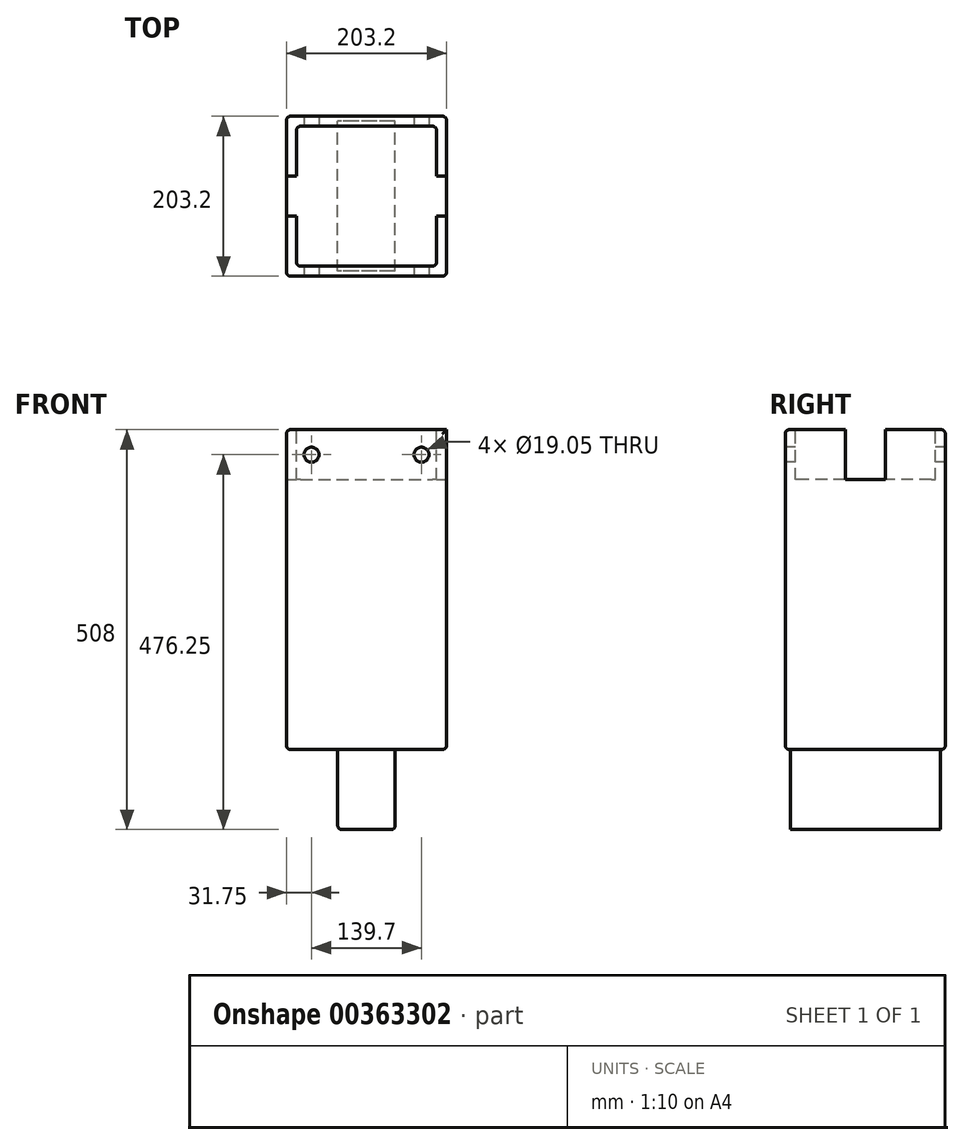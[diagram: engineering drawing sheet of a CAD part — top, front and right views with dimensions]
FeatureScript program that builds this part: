
annotation { "Feature Type Name" : "Feature", "Feature Type Description" : "" }
export const myFeature = defineFeature(function(context is Context, id is Id, definition is map)
    precondition{}
    {
        {
            var Q0;
            Q0=qCreatedBy(makeId("Top.planeOp"),FACE);
            var sketch = newSketch(context, id + "F0", { "sketchPlane" : qUnion([Q0])});
            skLineSegment(sketch, "E0.bottom", {"start": v(101.6, -101.6) * mm, "end": v(-101.6, -101.6) * mm});
            skLineSegment(sketch, "E0.top", {"start": v(101.6, 101.6) * mm, "end": v(-101.6, 101.6) * mm});
            skLineSegment(sketch, "E0.left", {"start": v(101.6, -101.6) * mm, "end": v(101.6, 101.6) * mm});
            skLineSegment(sketch, "E0.right", {"start": v(-101.6, -101.6) * mm, "end": v(-101.6, 101.6) * mm});
            skPoint(sketch, "E0.middle", {"position": v(0, 0) * mm});
            skSolve(sketch);
        }
        {
            var Q0;
            Q0=makeQuery(id+"F0.imprint","IMPRINT",FACE,{"disambiguationData":[TD([[makeQuery(id+"F0.imprint","IMPRINT",EDGE,{"derivedFrom":sQuery(id+"F0.wireOp",EDGE,"E0.bottom")}),-1.0]])]});
            extrude(context, id + "F1", {"entities" : qUnion([Q0]), "depth" : 406.4 * mm});
        }
        {
            var Q0;
            Q0=makeQuery(id+"F1.opExtrude","CAP_FACE",FACE,{"disambiguationData":[OSD([sQuery(id+"F0.wireOp",EDGE,"E0.bottom"),sQuery(id+"F0.wireOp",EDGE,"E0.top"),sQuery(id+"F0.wireOp",EDGE,"E0.left"),sQuery(id+"F0.wireOp",EDGE,"E0.right")])],"isStart":false});
            var sketch = newSketch(context, id + "F2", { "sketchPlane" : qUnion([Q0])});
            skLineSegment(sketch, "E1.0", {"start": v(101.6, -101.6) * mm, "end": v(101.6, 101.6) * mm});
            skLineSegment(sketch, "E1.2", {"start": v(101.6, 101.6) * mm, "end": v(-101.6, 101.6) * mm});
            skLineSegment(sketch, "E2.bottom", {"start": v(-88.9, 88.9) * mm, "end": v(88.9, 88.9) * mm});
            skLineSegment(sketch, "E2.top", {"start": v(-88.9, -88.9) * mm, "end": v(88.9, -88.9) * mm});
            skLineSegment(sketch, "E2.left", {"start": v(-88.9, 88.9) * mm, "end": v(-88.9, -88.9) * mm});
            skLineSegment(sketch, "E2.right", {"start": v(88.9, 88.9) * mm, "end": v(88.9, -88.9) * mm});
            skSolve(sketch);
        }
        {
            var Q0;
            Q0=makeQuery(id+"F2.imprint","IMPRINT",FACE,{"disambiguationData":[TD([[makeQuery(id+"F2.imprint","IMPRINT",EDGE,{"derivedFrom":sQuery(id+"F2.wireOp",EDGE,"E2.bottom")}),-1.0]])]});
            extrude(context, id + "F3", {"entities" : qUnion([Q0]), "operationType" : NewBodyOperationType.REMOVE, "oppositeDirection" : true, "depth" : 63.5 * mm});
        }
        {
            var Q0;
            Q0=makeQuery(id+"F1.opExtrude","SWEPT_FACE",FACE,{"disambiguationData":[OSD([sQuery(id+"F0.wireOp",EDGE,"E0.bottom")])]});
            var sketch = newSketch(context, id + "F4", { "sketchPlane" : qUnion([Q0])});
            skCircle(sketch, "E3", {"center": v(-69.85, 374.65) * mm, "radius": 9.53 * mm});
            skCircle(sketch, "E4", {"center": v(69.85, 374.65) * mm, "radius": 9.53 * mm});
            skSolve(sketch);
        }
        {
            var Q0;
            Q0=makeQuery(id+"F4.imprint","IMPRINT",FACE,{"disambiguationData":[TD([[makeQuery(id+"F4.imprint","IMPRINT",EDGE,{"derivedFrom":sQuery(id+"F4.wireOp",EDGE,"E3")}),1.0]])]});
            var Q1;
            Q1=makeQuery(id+"F4.imprint","IMPRINT",FACE,{"disambiguationData":[TD([[makeQuery(id+"F4.imprint","IMPRINT",EDGE,{"derivedFrom":sQuery(id+"F4.wireOp",EDGE,"E4")}),1.0]])]});
            extrude(context, id + "F5", {"entities" : qUnion([Q0, Q1]), "operationType" : NewBodyOperationType.REMOVE, "oppositeDirection" : true, "depth" : 205.74 * mm});
        }
        {
            var Q0;
            Q0=makeQuery(id+"F1.opExtrude","SWEPT_FACE",FACE,{"disambiguationData":[OSD([sQuery(id+"F0.wireOp",EDGE,"E0.left")])]});
            var sketch = newSketch(context, id + "F6", { "sketchPlane" : qUnion([Q0])});
            skLineSegment(sketch, "E5.bottom", {"start": v(-25.4, 406.4) * mm, "end": v(25.4, 406.4) * mm});
            skLineSegment(sketch, "E5.top", {"start": v(-25.4, 342.9) * mm, "end": v(25.4, 342.9) * mm});
            skLineSegment(sketch, "E5.left", {"start": v(-25.4, 406.4) * mm, "end": v(-25.4, 342.9) * mm});
            skLineSegment(sketch, "E5.right", {"start": v(25.4, 406.4) * mm, "end": v(25.4, 342.9) * mm});
            skPoint(sketch, "E5.middle", {"position": v(0, 374.65) * mm});
            skPoint(sketch, "E5.middle.positionSnap0", {"position": v(0, 406.4) * mm});
            skPoint(sketch, "E5.centerSnap0", {"position": v(0, 406.4) * mm});
            skSolve(sketch);
        }
        {
            var Q0;
            Q0 = qSketchRegion(id + "F6", true);
            extrude(context, id + "F7", {"entities" : qUnion([Q0]), "operationType" : NewBodyOperationType.REMOVE, "oppositeDirection" : true, "depth" : 228.6 * mm});
        }
        {
            var Q0;
            Q0=makeQuery(id+"F0.imprint","IMPRINT",FACE,{"disambiguationData":[TD([[makeQuery(id+"F0.imprint","IMPRINT",EDGE,{"derivedFrom":sQuery(id+"F0.wireOp",EDGE,"E0.bottom")}),-1.0]])]});
            var sketch = newSketch(context, id + "F8", { "sketchPlane" : qUnion([Q0])});
            skLineSegment(sketch, "E6.bottom", {"start": v(36.52, -95.25) * mm, "end": v(-36.52, -95.25) * mm});
            skLineSegment(sketch, "E6.top", {"start": v(36.52, 95.25) * mm, "end": v(-36.52, 95.25) * mm});
            skLineSegment(sketch, "E6.left", {"start": v(36.52, -95.25) * mm, "end": v(36.52, 95.25) * mm});
            skLineSegment(sketch, "E6.right", {"start": v(-36.52, -95.25) * mm, "end": v(-36.52, 95.25) * mm});
            skPoint(sketch, "E6.middle", {"position": v(0, 0) * mm});
            skSolve(sketch);
        }
        {
            var Q0;
            Q0=makeQuery(id+"F8.imprint","IMPRINT",FACE,{"disambiguationData":[TD([[makeQuery(id+"F8.imprint","IMPRINT",EDGE,{"derivedFrom":sQuery(id+"F8.wireOp",EDGE,"E6.bottom")}),-1.0]])]});
            extrude(context, id + "F9", {"entities" : qUnion([Q0]), "operationType" : NewBodyOperationType.ADD, "depth" : -101.6 * mm});
        }
        {
            var Q0;
            Q0=makeQuery(id+"F1.opExtrude","SWEPT_EDGE",EDGE,{"disambiguationData":[OSD([sQuery(id+"F0.wireOp",EDGE,"E0.top"),sQuery(id+"F0.wireOp",EDGE,"E0.right")])]});
            var Q1;
            Q1=makeQuery(id+"F1.opExtrude","SWEPT_EDGE",EDGE,{"disambiguationData":[OSD([sQuery(id+"F0.wireOp",EDGE,"E0.bottom"),sQuery(id+"F0.wireOp",EDGE,"E0.right")])]});
            var Q2;
            Q2=makeQuery(id+"F1.opExtrude","SWEPT_EDGE",EDGE,{"disambiguationData":[OSD([sQuery(id+"F0.wireOp",EDGE,"E0.top"),sQuery(id+"F0.wireOp",EDGE,"E0.left")])]});
            var Q3;
            {var subQ0=sQuery(id+"F0.wireOp",EDGE,"E0.left");var subQ1=sQuery(id+"F0.wireOp",EDGE,"E0.top");Q3=makeQuery(id+"F7.boolean.opBoolean","SPLIT",EDGE,{"disambiguationData":[TD([makeQuery(id+"F1.opExtrude","SWEPT_FACE",FACE,{"disambiguationData":[OSD([subQ1])]})])],"derivedFrom":makeQuery(id+"F1.opExtrude","CAP_EDGE",EDGE,{"disambiguationData":[OSD([subQ0])],"isStart":false})});}
            var Q4;
            Q4=makeQuery(id+"F1.opExtrude","CAP_EDGE",EDGE,{"disambiguationData":[OSD([sQuery(id+"F0.wireOp",EDGE,"E0.top")])],"isStart":false});
            var Q5;
            {var subQ0=sQuery(id+"F0.wireOp",EDGE,"E0.right");var subQ1=sQuery(id+"F0.wireOp",EDGE,"E0.top");Q5=makeQuery(id+"F7.boolean.opBoolean","SPLIT",EDGE,{"disambiguationData":[TD([makeQuery(id+"F1.opExtrude","SWEPT_FACE",FACE,{"disambiguationData":[OSD([subQ1])]})])],"derivedFrom":makeQuery(id+"F1.opExtrude","CAP_EDGE",EDGE,{"disambiguationData":[OSD([subQ0])],"isStart":false})});}
            var Q6;
            {var subQ0=sQuery(id+"F0.wireOp",EDGE,"E0.bottom");var subQ1=sQuery(id+"F0.wireOp",EDGE,"E0.right");Q6=makeQuery(id+"F7.boolean.opBoolean","SPLIT",EDGE,{"disambiguationData":[TD([makeQuery(id+"F1.opExtrude","SWEPT_FACE",FACE,{"disambiguationData":[OSD([subQ0])]})])],"derivedFrom":makeQuery(id+"F1.opExtrude","CAP_EDGE",EDGE,{"disambiguationData":[OSD([subQ1])],"isStart":false})});}
            var Q7;
            Q7=makeQuery(id+"F1.opExtrude","CAP_EDGE",EDGE,{"disambiguationData":[OSD([sQuery(id+"F0.wireOp",EDGE,"E0.bottom")])],"isStart":false});
            var Q8;
            Q8=makeQuery(id+"F1.opExtrude","SWEPT_EDGE",EDGE,{"disambiguationData":[OSD([sQuery(id+"F0.wireOp",EDGE,"E0.bottom"),sQuery(id+"F0.wireOp",EDGE,"E0.left")])]});
            var Q9;
            Q9=makeQuery(id+"F1.opExtrude","CAP_EDGE",EDGE,{"disambiguationData":[OSD([sQuery(id+"F0.wireOp",EDGE,"E0.left")])],"isStart":true});
            var Q10;
            Q10=makeQuery(id+"F1.opExtrude","CAP_EDGE",EDGE,{"disambiguationData":[OSD([sQuery(id+"F0.wireOp",EDGE,"E0.bottom")])],"isStart":true});
            var Q11;
            Q11=makeQuery(id+"F1.opExtrude","CAP_EDGE",EDGE,{"disambiguationData":[OSD([sQuery(id+"F0.wireOp",EDGE,"E0.top")])],"isStart":true});
            var Q12;
            Q12=makeQuery(id+"F1.opExtrude","CAP_EDGE",EDGE,{"disambiguationData":[OSD([sQuery(id+"F0.wireOp",EDGE,"E0.right")])],"isStart":true});
            var Q13;
            Q13=makeQuery(id+"F3.boolean.opBoolean","COPY",EDGE,{"derivedFrom":makeQuery(id+"F3.opExtrude","SWEPT_EDGE",EDGE,{"disambiguationData":[OSD([sQuery(id+"F2.wireOp",EDGE,"E2.top"),sQuery(id+"F2.wireOp",EDGE,"E2.left")])]})});
            var Q14;
            Q14=makeQuery(id+"F3.boolean.opBoolean","COPY",EDGE,{"derivedFrom":makeQuery(id+"F3.opExtrude","SWEPT_EDGE",EDGE,{"disambiguationData":[OSD([sQuery(id+"F2.wireOp",EDGE,"E2.bottom"),sQuery(id+"F2.wireOp",EDGE,"E2.left")])]})});
            var Q15;
            Q15=makeQuery(id+"F3.boolean.opBoolean","COPY",EDGE,{"derivedFrom":makeQuery(id+"F3.opExtrude","SWEPT_EDGE",EDGE,{"disambiguationData":[OSD([sQuery(id+"F2.wireOp",EDGE,"E2.top"),sQuery(id+"F2.wireOp",EDGE,"E2.right")])]})});
            var Q16;
            Q16=makeQuery(id+"F3.boolean.opBoolean","COPY",EDGE,{"derivedFrom":makeQuery(id+"F3.opExtrude","SWEPT_EDGE",EDGE,{"disambiguationData":[OSD([sQuery(id+"F2.wireOp",EDGE,"E2.bottom"),sQuery(id+"F2.wireOp",EDGE,"E2.right")])]})});
            var Q17;
            Q17=makeQuery(id+"F9.opExtrude","CAP_EDGE",EDGE,{"disambiguationData":[OSD([sQuery(id+"F8.wireOp",EDGE,"E6.left")])],"isStart":false});
            var Q18;
            Q18=makeQuery(id+"F9.opExtrude","CAP_EDGE",EDGE,{"disambiguationData":[OSD([sQuery(id+"F8.wireOp",EDGE,"E6.right")])],"isStart":false});
            fillet(context, id + "F10", {"entities" : qUnion([Q0, Q1, Q2, Q3, Q4, Q5, Q6, Q7, Q8, Q9, Q10, Q11, Q12, Q13, Q14, Q15, Q16, Q17, Q18]), "radius" : 5.08 * mm, "tangentPropagation" : true, "allowEdgeOverflow" : false});
        }
    });
